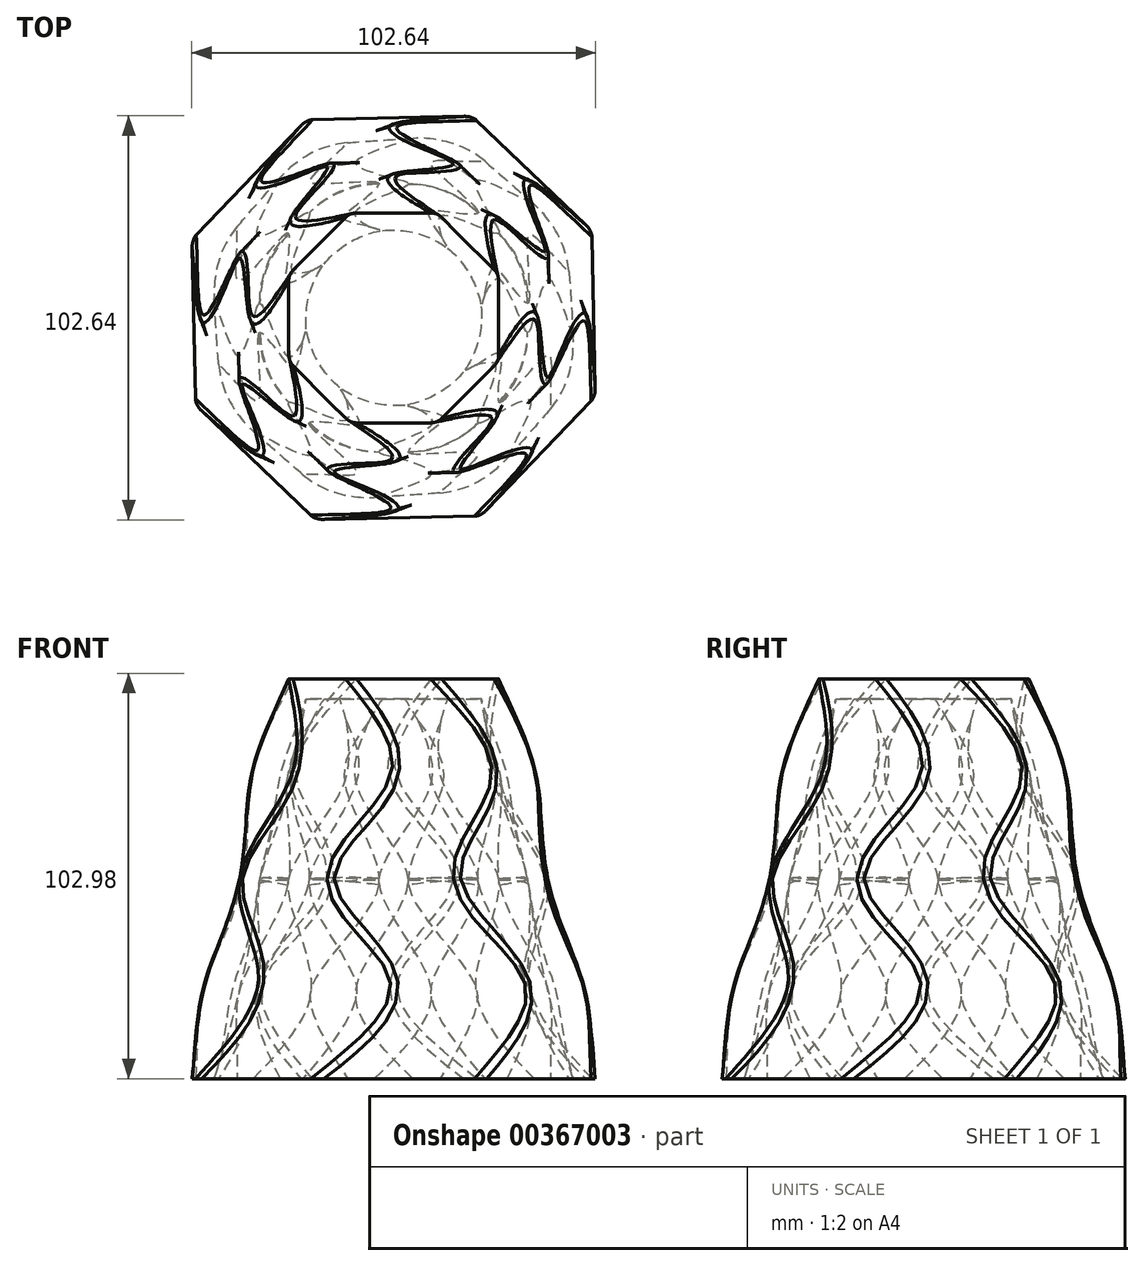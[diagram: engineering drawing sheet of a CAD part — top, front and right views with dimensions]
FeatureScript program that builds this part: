
annotation { "Feature Type Name" : "Feature", "Feature Type Description" : "" }
export const myFeature = defineFeature(function(context is Context, id is Id, definition is map)
    precondition{}
    {
        {
            var Q0;
            Q0=qCreatedBy(makeId("Top.planeOp"),FACE);
            cPlane(context, id + "F0", {"entities" : qUnion([Q0]), "cplaneType" : CPlaneType.OFFSET, "offset" : 50.8 * mm, "width" : 152.4 * mm, "height" : 152.4 * mm});
        }
        {
            var Q0;
            Q0=qCreatedBy(id+"F0.planeOp",FACE);
            var sketch = newSketch(context, id + "F1", { "sketchPlane" : qUnion([Q0])});
            skCircle(sketch, "E0.cCircle", {"center": v(0, 0) * mm, "radius": 26.67 * mm, "construction": true});
            skLineSegment(sketch, "E0.0", {"start": v(26.67, 11.05) * mm, "end": v(26.67, -11.05) * mm});
            skLineSegment(sketch, "E0.1", {"start": v(26.67, -11.05) * mm, "end": v(11.05, -26.67) * mm});
            skLineSegment(sketch, "E0.2", {"start": v(11.05, -26.67) * mm, "end": v(-11.05, -26.67) * mm});
            skLineSegment(sketch, "E0.3", {"start": v(-11.05, -26.67) * mm, "end": v(-26.67, -11.05) * mm});
            skLineSegment(sketch, "E0.4", {"start": v(-26.67, -11.05) * mm, "end": v(-26.67, 11.05) * mm});
            skLineSegment(sketch, "E0.5", {"start": v(-26.67, 11.05) * mm, "end": v(-11.05, 26.67) * mm});
            skLineSegment(sketch, "E0.6", {"start": v(-11.05, 26.67) * mm, "end": v(11.05, 26.67) * mm});
            skLineSegment(sketch, "E0.7", {"start": v(11.05, 26.67) * mm, "end": v(26.67, 11.05) * mm});
            skPoint(sketch, "E0.0.midPoint", {"position": v(26.67, 0) * mm});
            skSolve(sketch);
        }
        {
            var Q0;
            Q0=qCreatedBy(makeId("Top.planeOp"),FACE);
            cPlane(context, id + "F2", {"entities" : qUnion([Q0]), "cplaneType" : CPlaneType.OFFSET, "offset" : 50.8 * mm, "oppositeDirection" : true, "width" : 152.4 * mm, "height" : 152.4 * mm});
        }
        {
            var Q0;
            Q0=qCreatedBy(id+"F2.planeOp",FACE);
            var sketch = newSketch(context, id + "F3", { "sketchPlane" : qUnion([Q0])});
            skCircle(sketch, "E1.cCircle", {"center": v(0, 0) * mm, "radius": 50.8 * mm, "construction": true});
            skLineSegment(sketch, "E1.0", {"start": v(51.24, -19.95) * mm, "end": v(22.13, -50.34) * mm});
            skLineSegment(sketch, "E1.1", {"start": v(22.13, -50.34) * mm, "end": v(-19.95, -51.24) * mm});
            skLineSegment(sketch, "E1.2", {"start": v(-19.95, -51.24) * mm, "end": v(-50.34, -22.13) * mm});
            skLineSegment(sketch, "E1.3", {"start": v(-50.34, -22.13) * mm, "end": v(-51.24, 19.95) * mm});
            skLineSegment(sketch, "E1.4", {"start": v(-51.24, 19.95) * mm, "end": v(-22.13, 50.34) * mm});
            skLineSegment(sketch, "E1.5", {"start": v(-22.13, 50.34) * mm, "end": v(19.95, 51.24) * mm});
            skLineSegment(sketch, "E1.6", {"start": v(19.95, 51.24) * mm, "end": v(50.34, 22.13) * mm});
            skLineSegment(sketch, "E1.7", {"start": v(50.34, 22.13) * mm, "end": v(51.24, -19.95) * mm});
            skPoint(sketch, "E1.0.midPoint", {"position": v(36.68, -35.14) * mm});
            skSolve(sketch);
        }
        {
            var Q0;
            Q0=qCreatedBy(id+"F2.planeOp",FACE);
            cPlane(context, id + "F4", {"entities" : qUnion([Q0]), "cplaneType" : CPlaneType.OFFSET, "offset" : 25.4 * mm, "width" : 152.4 * mm, "height" : 152.4 * mm});
        }
        {
            var Q0;
            Q0=qCreatedBy(makeId("Top.planeOp"),FACE);
            cPlane(context, id + "F5", {"entities" : qUnion([Q0]), "cplaneType" : CPlaneType.OFFSET, "offset" : 25.4 * mm, "width" : 152.4 * mm, "height" : 152.4 * mm});
        }
        {
            var Q0;
            Q0=qCreatedBy(id+"F5.planeOp",FACE);
            var sketch = newSketch(context, id + "F6", { "sketchPlane" : qUnion([Q0])});
            skCircle(sketch, "E2.cCircle", {"center": v(0, 0) * mm, "radius": 33.83 * mm, "construction": true});
            skLineSegment(sketch, "E2.0", {"start": v(25.89, 25.89) * mm, "end": v(36.61, 0) * mm});
            skLineSegment(sketch, "E2.1", {"start": v(36.61, 0) * mm, "end": v(25.89, -25.89) * mm});
            skLineSegment(sketch, "E2.2", {"start": v(25.89, -25.89) * mm, "end": v(0, -36.61) * mm});
            skLineSegment(sketch, "E2.3", {"start": v(0, -36.61) * mm, "end": v(-25.89, -25.89) * mm});
            skLineSegment(sketch, "E2.4", {"start": v(-25.89, -25.89) * mm, "end": v(-36.61, 0) * mm});
            skLineSegment(sketch, "E2.5", {"start": v(-36.61, 0) * mm, "end": v(-25.89, 25.89) * mm});
            skLineSegment(sketch, "E2.6", {"start": v(-25.89, 25.89) * mm, "end": v(0, 36.61) * mm});
            skLineSegment(sketch, "E2.7", {"start": v(0, 36.61) * mm, "end": v(25.89, 25.89) * mm});
            skPoint(sketch, "E2.0.midPoint", {"position": v(31.25, 12.94) * mm});
            skSolve(sketch);
        }
        {
            var Q0;
            Q0=qCreatedBy(makeId("Top.planeOp"),FACE);
            var sketch = newSketch(context, id + "F7", { "sketchPlane" : qUnion([Q0])});
            skCircle(sketch, "E3.cCircle", {"center": v(0, 0) * mm, "radius": 39.14 * mm, "construction": true});
            skLineSegment(sketch, "E3.0", {"start": v(-16.21, 39.14) * mm, "end": v(16.21, 39.14) * mm});
            skLineSegment(sketch, "E3.1", {"start": v(16.21, 39.14) * mm, "end": v(39.14, 16.21) * mm});
            skLineSegment(sketch, "E3.2", {"start": v(39.14, 16.21) * mm, "end": v(39.14, -16.21) * mm});
            skLineSegment(sketch, "E3.3", {"start": v(39.14, -16.21) * mm, "end": v(16.21, -39.14) * mm});
            skLineSegment(sketch, "E3.4", {"start": v(16.21, -39.14) * mm, "end": v(-16.21, -39.14) * mm});
            skLineSegment(sketch, "E3.5", {"start": v(-16.21, -39.14) * mm, "end": v(-39.14, -16.21) * mm});
            skLineSegment(sketch, "E3.6", {"start": v(-39.14, -16.21) * mm, "end": v(-39.14, 16.21) * mm});
            skLineSegment(sketch, "E3.7", {"start": v(-39.14, 16.21) * mm, "end": v(-16.21, 39.14) * mm});
            skPoint(sketch, "E3.0.midPoint", {"position": v(0, 39.14) * mm});
            skSolve(sketch);
        }
        {
            var Q0;
            Q0=qCreatedBy(id+"F4.planeOp",FACE);
            var sketch = newSketch(context, id + "F8", { "sketchPlane" : qUnion([Q0])});
            skCircle(sketch, "E4.cCircle", {"center": v(0, 0) * mm, "radius": 44.32 * mm, "construction": true});
            skLineSegment(sketch, "E4.0", {"start": v(0, 47.97) * mm, "end": v(33.92, 33.92) * mm});
            skLineSegment(sketch, "E4.1", {"start": v(33.92, 33.92) * mm, "end": v(47.97, 0) * mm});
            skLineSegment(sketch, "E4.2", {"start": v(47.97, 0) * mm, "end": v(33.92, -33.92) * mm});
            skLineSegment(sketch, "E4.3", {"start": v(33.92, -33.92) * mm, "end": v(0, -47.97) * mm});
            skLineSegment(sketch, "E4.4", {"start": v(0, -47.97) * mm, "end": v(-33.92, -33.92) * mm});
            skLineSegment(sketch, "E4.5", {"start": v(-33.92, -33.92) * mm, "end": v(-47.97, 0) * mm});
            skLineSegment(sketch, "E4.6", {"start": v(-47.97, 0) * mm, "end": v(-33.92, 33.92) * mm});
            skLineSegment(sketch, "E4.7", {"start": v(-33.92, 33.92) * mm, "end": v(0, 47.97) * mm});
            skPoint(sketch, "E4.0.midPoint", {"position": v(16.96, 40.95) * mm});
            skSolve(sketch);
        }
        {
            var Q0;
            Q0=makeQuery(id+"F1.imprint","IMPRINT",FACE,{"disambiguationData":[TD([[makeQuery(id+"F1.imprint","IMPRINT",EDGE,{"derivedFrom":sQuery(id+"F1.wireOp",EDGE,"E0.0")}),-1.0]])]});
            var Q1;
            Q1=makeQuery(id+"F6.imprint","IMPRINT",FACE,{"disambiguationData":[TD([[makeQuery(id+"F6.imprint","IMPRINT",EDGE,{"derivedFrom":sQuery(id+"F6.wireOp",EDGE,"E2.0")}),-1.0]])]});
            var Q2;
            Q2=makeQuery(id+"F7.imprint","IMPRINT",FACE,{"disambiguationData":[TD([[makeQuery(id+"F7.imprint","IMPRINT",EDGE,{"derivedFrom":sQuery(id+"F7.wireOp",EDGE,"E3.0")}),-1.0]])]});
            var Q3;
            Q3=makeQuery(id+"F8.imprint","IMPRINT",FACE,{"disambiguationData":[TD([[makeQuery(id+"F8.imprint","IMPRINT",EDGE,{"derivedFrom":sQuery(id+"F8.wireOp",EDGE,"E4.0")}),-1.0]])]});
            var Q4;
            Q4=makeQuery(id+"F3.imprint","IMPRINT",FACE,{"disambiguationData":[TD([[makeQuery(id+"F3.imprint","IMPRINT",EDGE,{"derivedFrom":sQuery(id+"F3.wireOp",EDGE,"E1.0")}),-1.0]])]});
            loft(context, id + "F9", {"sheetProfilesArray" : [{ "sheetProfileEntities" : qUnion([Q0]) }, { "sheetProfileEntities" : qUnion([Q1]) }, { "sheetProfileEntities" : qUnion([Q2]) }, { "sheetProfileEntities" : qUnion([Q3]) }, { "sheetProfileEntities" : qUnion([Q4]) }]});
        }
        {
            var Q0;
            Q0=makeQuery(id+"F9.opLoft","CAP_FACE",FACE,{"disambiguationData":[OSD([makeQuery(id+"F3.imprint","IMPRINT",FACE,{"disambiguationData":[TD([[makeQuery(id+"F3.imprint","IMPRINT",EDGE,{"derivedFrom":sQuery(id+"F3.wireOp",EDGE,"E1.0")}),-1.0]])]})])],"isStart":true});
            shell(context, id + "F10", {"entities" : qUnion([Q0]), "thickness" : 5.08 * mm});
        }
        {
            var Q0;
            Q0=makeQuery(id+"F10.opShell","OFFSET_EDGE",EDGE,{"disambiguationData":[OSD([sQuery(id+"F1.wireOp",EDGE,"E0.0"),sQuery(id+"F1.wireOp",EDGE,"E0.7"),sQuery(id+"F3.wireOp",EDGE,"E1.6"),sQuery(id+"F3.wireOp",EDGE,"E1.7"),sQuery(id+"F6.wireOp",EDGE,"E2.0"),sQuery(id+"F6.wireOp",EDGE,"E2.7"),sQuery(id+"F7.wireOp",EDGE,"E3.1"),sQuery(id+"F7.wireOp",EDGE,"E3.2"),sQuery(id+"F8.wireOp",EDGE,"E4.0"),sQuery(id+"F8.wireOp",EDGE,"E4.1")])]});
            var Q1;
            Q1=makeQuery(id+"F10.opShell","OFFSET_EDGE",EDGE,{"disambiguationData":[OSD([sQuery(id+"F1.wireOp",EDGE,"E0.6"),sQuery(id+"F1.wireOp",EDGE,"E0.7"),sQuery(id+"F3.wireOp",EDGE,"E1.5"),sQuery(id+"F3.wireOp",EDGE,"E1.6"),sQuery(id+"F6.wireOp",EDGE,"E2.6"),sQuery(id+"F6.wireOp",EDGE,"E2.7"),sQuery(id+"F7.wireOp",EDGE,"E3.0"),sQuery(id+"F7.wireOp",EDGE,"E3.1"),sQuery(id+"F8.wireOp",EDGE,"E4.0"),sQuery(id+"F8.wireOp",EDGE,"E4.7")])]});
            var Q2;
            Q2=makeQuery(id+"F10.opShell","OFFSET_EDGE",EDGE,{"disambiguationData":[OSD([sQuery(id+"F1.wireOp",EDGE,"E0.5"),sQuery(id+"F1.wireOp",EDGE,"E0.6"),sQuery(id+"F3.wireOp",EDGE,"E1.4"),sQuery(id+"F3.wireOp",EDGE,"E1.5"),sQuery(id+"F6.wireOp",EDGE,"E2.5"),sQuery(id+"F6.wireOp",EDGE,"E2.6"),sQuery(id+"F7.wireOp",EDGE,"E3.0"),sQuery(id+"F7.wireOp",EDGE,"E3.7"),sQuery(id+"F8.wireOp",EDGE,"E4.6"),sQuery(id+"F8.wireOp",EDGE,"E4.7")])]});
            var Q3;
            Q3=makeQuery(id+"F10.opShell","OFFSET_EDGE",EDGE,{"disambiguationData":[OSD([sQuery(id+"F1.wireOp",EDGE,"E0.0"),sQuery(id+"F1.wireOp",EDGE,"E0.1"),sQuery(id+"F3.wireOp",EDGE,"E1.0"),sQuery(id+"F3.wireOp",EDGE,"E1.7"),sQuery(id+"F6.wireOp",EDGE,"E2.0"),sQuery(id+"F6.wireOp",EDGE,"E2.1"),sQuery(id+"F7.wireOp",EDGE,"E3.2"),sQuery(id+"F7.wireOp",EDGE,"E3.3"),sQuery(id+"F8.wireOp",EDGE,"E4.1"),sQuery(id+"F8.wireOp",EDGE,"E4.2")])]});
            var Q4;
            Q4=makeQuery(id+"F10.opShell","OFFSET_EDGE",EDGE,{"disambiguationData":[OSD([sQuery(id+"F1.wireOp",EDGE,"E0.1"),sQuery(id+"F1.wireOp",EDGE,"E0.2"),sQuery(id+"F3.wireOp",EDGE,"E1.0"),sQuery(id+"F3.wireOp",EDGE,"E1.1"),sQuery(id+"F6.wireOp",EDGE,"E2.1"),sQuery(id+"F6.wireOp",EDGE,"E2.2"),sQuery(id+"F7.wireOp",EDGE,"E3.3"),sQuery(id+"F7.wireOp",EDGE,"E3.4"),sQuery(id+"F8.wireOp",EDGE,"E4.2"),sQuery(id+"F8.wireOp",EDGE,"E4.3")])]});
            var Q5;
            Q5=makeQuery(id+"F10.opShell","OFFSET_EDGE",EDGE,{"disambiguationData":[OSD([sQuery(id+"F1.wireOp",EDGE,"E0.2"),sQuery(id+"F1.wireOp",EDGE,"E0.3"),sQuery(id+"F3.wireOp",EDGE,"E1.1"),sQuery(id+"F3.wireOp",EDGE,"E1.2"),sQuery(id+"F6.wireOp",EDGE,"E2.2"),sQuery(id+"F6.wireOp",EDGE,"E2.3"),sQuery(id+"F7.wireOp",EDGE,"E3.4"),sQuery(id+"F7.wireOp",EDGE,"E3.5"),sQuery(id+"F8.wireOp",EDGE,"E4.3"),sQuery(id+"F8.wireOp",EDGE,"E4.4")])]});
            var Q6;
            Q6=makeQuery(id+"F10.opShell","OFFSET_EDGE",EDGE,{"disambiguationData":[OSD([sQuery(id+"F1.wireOp",EDGE,"E0.4"),sQuery(id+"F1.wireOp",EDGE,"E0.5"),sQuery(id+"F3.wireOp",EDGE,"E1.3"),sQuery(id+"F3.wireOp",EDGE,"E1.4"),sQuery(id+"F6.wireOp",EDGE,"E2.4"),sQuery(id+"F6.wireOp",EDGE,"E2.5"),sQuery(id+"F7.wireOp",EDGE,"E3.6"),sQuery(id+"F7.wireOp",EDGE,"E3.7"),sQuery(id+"F8.wireOp",EDGE,"E4.5"),sQuery(id+"F8.wireOp",EDGE,"E4.6")])]});
            var Q7;
            Q7=makeQuery(id+"F10.opShell","OFFSET_EDGE",EDGE,{"disambiguationData":[OSD([sQuery(id+"F1.wireOp",EDGE,"E0.3"),sQuery(id+"F1.wireOp",EDGE,"E0.4"),sQuery(id+"F3.wireOp",EDGE,"E1.2"),sQuery(id+"F3.wireOp",EDGE,"E1.3"),sQuery(id+"F6.wireOp",EDGE,"E2.3"),sQuery(id+"F6.wireOp",EDGE,"E2.4"),sQuery(id+"F7.wireOp",EDGE,"E3.5"),sQuery(id+"F7.wireOp",EDGE,"E3.6"),sQuery(id+"F8.wireOp",EDGE,"E4.4"),sQuery(id+"F8.wireOp",EDGE,"E4.5")])]});
            fillet(context, id + "F11", {"entities" : qUnion([Q0, Q1, Q2, Q3, Q4, Q5, Q6, Q7]), "radius" : 25.4 * mm, "tangentPropagation" : true, "allowEdgeOverflow" : false});
        }
        {
            var Q0;
            Q0=makeQuery(id+"F9.opLoft","SWEPT_EDGE",EDGE,{"disambiguationData":[OSD([sQuery(id+"F1.wireOp",EDGE,"E0.0"),sQuery(id+"F1.wireOp",EDGE,"E0.1"),sQuery(id+"F3.wireOp",EDGE,"E1.0"),sQuery(id+"F3.wireOp",EDGE,"E1.7"),sQuery(id+"F6.wireOp",EDGE,"E2.0"),sQuery(id+"F6.wireOp",EDGE,"E2.1"),sQuery(id+"F7.wireOp",EDGE,"E3.2"),sQuery(id+"F7.wireOp",EDGE,"E3.3"),sQuery(id+"F8.wireOp",EDGE,"E4.1"),sQuery(id+"F8.wireOp",EDGE,"E4.2")])]});
            var Q1;
            Q1=makeQuery(id+"F9.opLoft","SWEPT_EDGE",EDGE,{"disambiguationData":[OSD([sQuery(id+"F1.wireOp",EDGE,"E0.1"),sQuery(id+"F1.wireOp",EDGE,"E0.2"),sQuery(id+"F3.wireOp",EDGE,"E1.0"),sQuery(id+"F3.wireOp",EDGE,"E1.1"),sQuery(id+"F6.wireOp",EDGE,"E2.1"),sQuery(id+"F6.wireOp",EDGE,"E2.2"),sQuery(id+"F7.wireOp",EDGE,"E3.3"),sQuery(id+"F7.wireOp",EDGE,"E3.4"),sQuery(id+"F8.wireOp",EDGE,"E4.2"),sQuery(id+"F8.wireOp",EDGE,"E4.3")])]});
            var Q2;
            Q2=makeQuery(id+"F9.opLoft","SWEPT_EDGE",EDGE,{"disambiguationData":[OSD([sQuery(id+"F1.wireOp",EDGE,"E0.2"),sQuery(id+"F1.wireOp",EDGE,"E0.3"),sQuery(id+"F3.wireOp",EDGE,"E1.1"),sQuery(id+"F3.wireOp",EDGE,"E1.2"),sQuery(id+"F6.wireOp",EDGE,"E2.2"),sQuery(id+"F6.wireOp",EDGE,"E2.3"),sQuery(id+"F7.wireOp",EDGE,"E3.4"),sQuery(id+"F7.wireOp",EDGE,"E3.5"),sQuery(id+"F8.wireOp",EDGE,"E4.3"),sQuery(id+"F8.wireOp",EDGE,"E4.4")])]});
            var Q3;
            Q3=makeQuery(id+"F9.opLoft","SWEPT_EDGE",EDGE,{"disambiguationData":[OSD([sQuery(id+"F1.wireOp",EDGE,"E0.3"),sQuery(id+"F1.wireOp",EDGE,"E0.4"),sQuery(id+"F3.wireOp",EDGE,"E1.2"),sQuery(id+"F3.wireOp",EDGE,"E1.3"),sQuery(id+"F6.wireOp",EDGE,"E2.3"),sQuery(id+"F6.wireOp",EDGE,"E2.4"),sQuery(id+"F7.wireOp",EDGE,"E3.5"),sQuery(id+"F7.wireOp",EDGE,"E3.6"),sQuery(id+"F8.wireOp",EDGE,"E4.4"),sQuery(id+"F8.wireOp",EDGE,"E4.5")])]});
            var Q4;
            Q4=makeQuery(id+"F9.opLoft","SWEPT_EDGE",EDGE,{"disambiguationData":[OSD([sQuery(id+"F1.wireOp",EDGE,"E0.4"),sQuery(id+"F1.wireOp",EDGE,"E0.5"),sQuery(id+"F3.wireOp",EDGE,"E1.3"),sQuery(id+"F3.wireOp",EDGE,"E1.4"),sQuery(id+"F6.wireOp",EDGE,"E2.4"),sQuery(id+"F6.wireOp",EDGE,"E2.5"),sQuery(id+"F7.wireOp",EDGE,"E3.6"),sQuery(id+"F7.wireOp",EDGE,"E3.7"),sQuery(id+"F8.wireOp",EDGE,"E4.5"),sQuery(id+"F8.wireOp",EDGE,"E4.6")])]});
            var Q5;
            Q5=makeQuery(id+"F9.opLoft","SWEPT_EDGE",EDGE,{"disambiguationData":[OSD([sQuery(id+"F1.wireOp",EDGE,"E0.0"),sQuery(id+"F1.wireOp",EDGE,"E0.7"),sQuery(id+"F3.wireOp",EDGE,"E1.6"),sQuery(id+"F3.wireOp",EDGE,"E1.7"),sQuery(id+"F6.wireOp",EDGE,"E2.0"),sQuery(id+"F6.wireOp",EDGE,"E2.7"),sQuery(id+"F7.wireOp",EDGE,"E3.1"),sQuery(id+"F7.wireOp",EDGE,"E3.2"),sQuery(id+"F8.wireOp",EDGE,"E4.0"),sQuery(id+"F8.wireOp",EDGE,"E4.1")])]});
            var Q6;
            Q6=makeQuery(id+"F9.opLoft","SWEPT_EDGE",EDGE,{"disambiguationData":[OSD([sQuery(id+"F1.wireOp",EDGE,"E0.6"),sQuery(id+"F1.wireOp",EDGE,"E0.7"),sQuery(id+"F3.wireOp",EDGE,"E1.5"),sQuery(id+"F3.wireOp",EDGE,"E1.6"),sQuery(id+"F6.wireOp",EDGE,"E2.6"),sQuery(id+"F6.wireOp",EDGE,"E2.7"),sQuery(id+"F7.wireOp",EDGE,"E3.0"),sQuery(id+"F7.wireOp",EDGE,"E3.1"),sQuery(id+"F8.wireOp",EDGE,"E4.0"),sQuery(id+"F8.wireOp",EDGE,"E4.7")])]});
            var Q7;
            Q7=makeQuery(id+"F9.opLoft","SWEPT_EDGE",EDGE,{"disambiguationData":[OSD([sQuery(id+"F1.wireOp",EDGE,"E0.5"),sQuery(id+"F1.wireOp",EDGE,"E0.6"),sQuery(id+"F3.wireOp",EDGE,"E1.4"),sQuery(id+"F3.wireOp",EDGE,"E1.5"),sQuery(id+"F6.wireOp",EDGE,"E2.5"),sQuery(id+"F6.wireOp",EDGE,"E2.6"),sQuery(id+"F7.wireOp",EDGE,"E3.0"),sQuery(id+"F7.wireOp",EDGE,"E3.7"),sQuery(id+"F8.wireOp",EDGE,"E4.6"),sQuery(id+"F8.wireOp",EDGE,"E4.7")])]});
            fillet(context, id + "F12", {"entities" : qUnion([Q0, Q1, Q2, Q3, Q4, Q5, Q6, Q7]), "radius" : 2.54 * mm, "tangentPropagation" : true, "allowEdgeOverflow" : false});
        }
    });
